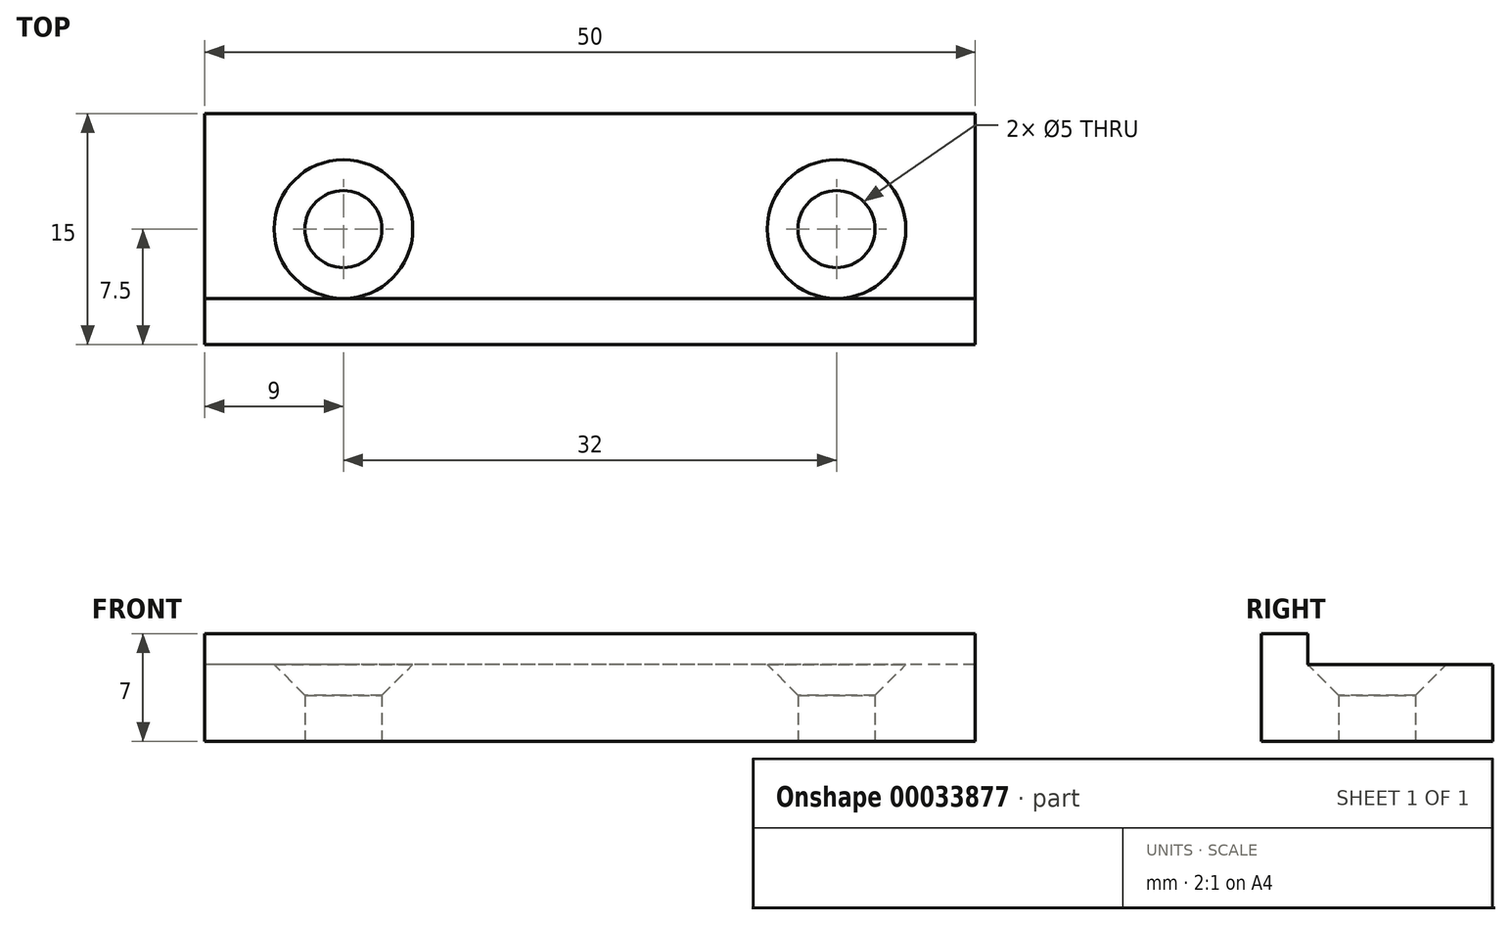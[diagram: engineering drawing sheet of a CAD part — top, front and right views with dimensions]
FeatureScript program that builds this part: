
annotation { "Feature Type Name" : "Feature", "Feature Type Description" : "" }
export const myFeature = defineFeature(function(context is Context, id is Id, definition is map)
    precondition{}
    {
        {
            var Q0;
            Q0=qCreatedBy(makeId("Right.planeOp"),FACE);
            var sketch = newSketch(context, id + "F0", { "sketchPlane" : qUnion([Q0])});
            skLineSegment(sketch, "E0.bottom", {"start": v(0, 0) * mm, "end": v(-15, 0) * mm});
            skLineSegment(sketch, "E0.top", {"start": v(0, 5) * mm, "end": v(-12, 5) * mm});
            skLineSegment(sketch, "E0.left", {"start": v(0, 0) * mm, "end": v(0, 5) * mm});
            skLineSegment(sketch, "E0.right", {"start": v(-15, 0) * mm, "end": v(-15, 5) * mm});
            skLineSegment(sketch, "E1.top", {"start": v(-15, 7) * mm, "end": v(-12, 7) * mm});
            skLineSegment(sketch, "E1.left", {"start": v(-15, 5) * mm, "end": v(-15, 7) * mm});
            skLineSegment(sketch, "E1.right", {"start": v(-12, 5) * mm, "end": v(-12, 7) * mm});
            skSolve(sketch);
        }
        {
            var Q0;
            Q0 = qSketchRegion(id + "F0", true);
            extrude(context, id + "F1", {"entities" : qUnion([Q0]), "depth" : 50 * mm});
        }
        {
            var Q0;
            Q0=makeQuery(id+"F1.opExtrude","SWEPT_FACE",FACE,{"disambiguationData":[OSD([sQuery(id+"F0.wireOp",EDGE,"E0.top")])]});
            var sketch = newSketch(context, id + "F2", { "sketchPlane" : qUnion([Q0])});
            skPoint(sketch, "E2", {"position": v(41, -7.5) * mm});
            skPoint(sketch, "E3", {"position": v(9, -7.5) * mm});
            skLineSegment(sketch, "E4", {"start": v(41, -7.5) * mm, "end": v(9, -7.5) * mm, "construction": true});
            skPoint(sketch, "E5", {"position": v(25, 0) * mm});
            skPoint(sketch, "E6", {"position": v(25, -7.5) * mm});
            skSolve(sketch);
        }
        {
            var Q0;
            Q0=sQuery(id+"F2.wireOp",VERTEX,"E2");
            var Q1;
            Q1=sQuery(id+"F2.wireOp",VERTEX,"E3");
            var Q2;
            Q2=makeQuery(id+"F1.opExtrude","SWEPT_BODY",BODY,{"disambiguationData":[OSD([sQuery(id+"F0.wireOp",EDGE,"E0.bottom"),sQuery(id+"F0.wireOp",EDGE,"E0.top"),sQuery(id+"F0.wireOp",EDGE,"E0.left"),sQuery(id+"F0.wireOp",EDGE,"E0.right"),sQuery(id+"F0.wireOp",EDGE,"E1.top"),sQuery(id+"F0.wireOp",EDGE,"E1.left"),sQuery(id+"F0.wireOp",EDGE,"E1.right")])]});
            hole(context, id + "F3", {"style" : HoleStyle.C_SINK, "holeDiameter" : 5 * mm, "cSinkDiameter" : 9 * mm, "endStyle" : HoleEndStyle.THROUGH, "locations" : qUnion([Q0, Q1]), "scope" : qUnion([Q2]), "cSinkAngle" : 90 * degree});
        }
    });
